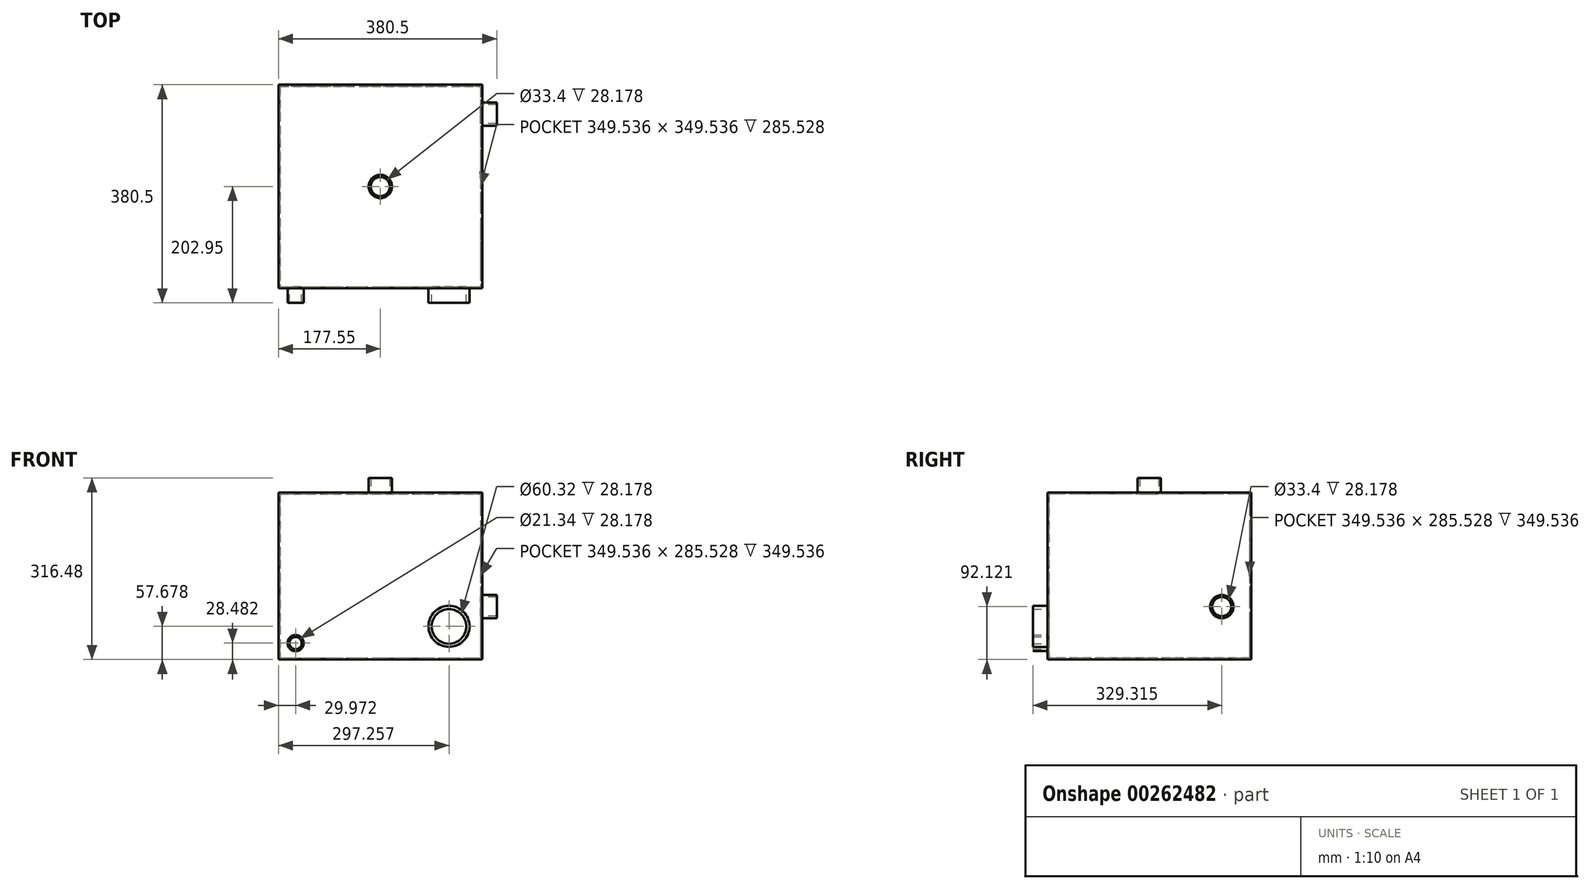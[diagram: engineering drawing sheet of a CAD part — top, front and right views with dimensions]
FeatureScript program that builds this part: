
annotation { "Feature Type Name" : "Feature", "Feature Type Description" : "" }
export const myFeature = defineFeature(function(context is Context, id is Id, definition is map)
    precondition{}
    {
        {
            var Q0;
            Q0=qCreatedBy(makeId("Top.planeOp"),FACE);
            var sketch = newSketch(context, id + "F0", { "sketchPlane" : qUnion([Q0])});
            skLineSegment(sketch, "E0.bottom", {"start": v(-177.55, 177.55) * mm, "end": v(177.55, 177.55) * mm});
            skLineSegment(sketch, "E0.top", {"start": v(-177.55, -177.55) * mm, "end": v(177.55, -177.55) * mm});
            skLineSegment(sketch, "E0.left", {"start": v(-177.55, 177.55) * mm, "end": v(-177.55, -177.55) * mm});
            skLineSegment(sketch, "E0.right", {"start": v(177.55, 177.55) * mm, "end": v(177.55, -177.55) * mm});
            skPoint(sketch, "E0.middle", {"position": v(0, 0) * mm});
            skLineSegment(sketch, "E1.0", {"start": v(174.77, 174.77) * mm, "end": v(174.77, -174.77) * mm});
            skLineSegment(sketch, "E1.1", {"start": v(-174.77, 174.77) * mm, "end": v(174.77, 174.77) * mm});
            skLineSegment(sketch, "E1.2", {"start": v(-174.77, 174.77) * mm, "end": v(-174.77, -174.77) * mm});
            skLineSegment(sketch, "E1.3", {"start": v(-174.77, -174.77) * mm, "end": v(174.77, -174.77) * mm});
            skSolve(sketch);
        }
        {
            var Q0;
            Q0 = qSketchRegion(id + "F0", true);
            extrude(context, id + "F1", {"entities" : qUnion([Q0]), "depth" : 291.08 * mm});
        }
        {
            var Q0;
            Q0=qCreatedBy(makeId("Top.planeOp"),FACE);
            var sketch = newSketch(context, id + "F2", { "sketchPlane" : qUnion([Q0])});
            skLineSegment(sketch, "E2.0", {"start": v(-174.77, 174.77) * mm, "end": v(174.77, 174.77) * mm});
            skLineSegment(sketch, "E2.1", {"start": v(-174.77, 174.77) * mm, "end": v(-174.77, -174.77) * mm});
            skLineSegment(sketch, "E2.2", {"start": v(-174.77, -174.77) * mm, "end": v(174.77, -174.77) * mm});
            skLineSegment(sketch, "E2.3", {"start": v(174.77, 174.77) * mm, "end": v(174.77, -174.77) * mm});
            skSolve(sketch);
        }
        {
            var Q0;
            Q0 = qSketchRegion(id + "F2", true);
            extrude(context, id + "F3", {"entities" : qUnion([Q0]), "operationType" : NewBodyOperationType.ADD, "depth" : 2.78 * mm});
        }
        {
            var Q0;
            Q0=makeQuery(id+"F1.opExtrude","SWEPT_FACE",FACE,{"disambiguationData":[OSD([sQuery(id+"F0.wireOp",EDGE,"E0.top")])]});
            var sketch = newSketch(context, id + "F4", { "sketchPlane" : qUnion([Q0])});
            skCircle(sketch, "E3", {"center": v(119.7, 57.68) * mm, "radius": 30.16 * mm});
            skCircle(sketch, "E4", {"center": v(119.7, 57.68) * mm, "radius": 35.77 * mm});
            skSolve(sketch);
        }
        {
            var Q0;
            Q0 = qSketchRegion(id + "F4", true);
            extrude(context, id + "F5", {"entities" : qUnion([Q0]), "operationType" : NewBodyOperationType.ADD, "depth" : 25.4 * mm});
        }
        {
            var Q0;
            Q0=makeQuery(id+"F5.boolean.opBoolean","SPLIT",FACE,{"disambiguationData":[TD([makeQuery(id+"F5.opExtrude","SWEPT_FACE",FACE,{"disambiguationData":[OSD([sQuery(id+"F4.wireOp",EDGE,"w2y7WUbF-v39G-EkZH-f1oj-RHrdTK3vwLKV")])]})])],"derivedFrom":makeQuery(id+"F1.opExtrude","SWEPT_FACE",FACE,{"disambiguationData":[OSD([sQuery(id+"F0.wireOp",EDGE,"E0.top")])]})});
            var Q1;
            Q1=makeQuery(id+"F5.boolean.opBoolean","SPLIT",FACE,{"disambiguationData":[TD([makeQuery(id+"F5.opExtrude","SWEPT_FACE",FACE,{"disambiguationData":[OSD([sQuery(id+"F4.wireOp",EDGE,"E3")])]})])],"derivedFrom":makeQuery(id+"F1.opExtrude","SWEPT_FACE",FACE,{"disambiguationData":[OSD([sQuery(id+"F0.wireOp",EDGE,"E0.top")])]})});
            extrude(context, id + "F6", {"entities" : qUnion([Q0, Q1]), "operationType" : NewBodyOperationType.REMOVE, "oppositeDirection" : true, "depth" : 25.4 * mm});
        }
        {
            var Q0;
            Q0=makeQuery(id+"F1.opExtrude","SWEPT_FACE",FACE,{"disambiguationData":[OSD([sQuery(id+"F0.wireOp",EDGE,"E0.right")])]});
            var sketch = newSketch(context, id + "F7", { "sketchPlane" : qUnion([Q0])});
            skCircle(sketch, "E5", {"center": v(126.36, 92.12) * mm, "radius": 16.7 * mm});
            skCircle(sketch, "E6", {"center": v(126.36, 92.12) * mm, "radius": 20.3 * mm});
            skSolve(sketch);
        }
        {
            var Q0;
            Q0 = qSketchRegion(id + "F7", true);
            extrude(context, id + "F8", {"entities" : qUnion([Q0]), "operationType" : NewBodyOperationType.ADD, "depth" : 25.4 * mm});
        }
        {
            var Q0;
            Q0=makeQuery(id+"F8.boolean.opBoolean","SPLIT",FACE,{"disambiguationData":[TD([makeQuery(id+"F8.opExtrude","SWEPT_FACE",FACE,{"disambiguationData":[OSD([sQuery(id+"F7.wireOp",EDGE,"E5")])]})])],"derivedFrom":makeQuery(id+"F1.opExtrude","SWEPT_FACE",FACE,{"disambiguationData":[OSD([sQuery(id+"F0.wireOp",EDGE,"E0.right")])]})});
            extrude(context, id + "F9", {"entities" : qUnion([Q0]), "operationType" : NewBodyOperationType.REMOVE, "oppositeDirection" : true, "depth" : 25.4 * mm});
        }
        {
            var Q0;
            {var subQ1=sQuery(id+"F0.wireOp",EDGE,"E0.left");var subQ6=sQuery(id+"F0.wireOp",EDGE,"E0.top");Q0=makeQuery(id+"F5.boolean.opBoolean","SPLIT",FACE,{"disambiguationData":[TD([makeQuery(id+"F1.opExtrude","SWEPT_FACE",FACE,{"disambiguationData":[OSD([subQ1])]})])],"derivedFrom":makeQuery(id+"F1.opExtrude","SWEPT_FACE",FACE,{"disambiguationData":[OSD([subQ6])]})});}
            var sketch = newSketch(context, id + "F10", { "sketchPlane" : qUnion([Q0])});
            skCircle(sketch, "E7", {"center": v(-147.58, 28.48) * mm, "radius": 10.67 * mm});
            skCircle(sketch, "E8", {"center": v(-147.58, 28.48) * mm, "radius": 14.06 * mm});
            skSolve(sketch);
        }
        {
            var Q0;
            Q0 = qSketchRegion(id + "F10", true);
            extrude(context, id + "F11", {"entities" : qUnion([Q0]), "operationType" : NewBodyOperationType.ADD, "depth" : 25.4 * mm});
        }
        {
            var Q0;
            {var subQ1=sQuery(id+"F0.wireOp",EDGE,"E0.left");var subQ6=sQuery(id+"F0.wireOp",EDGE,"E0.top");Q0=makeQuery(id+"F11.boolean.opBoolean","SPLIT",FACE,{"disambiguationData":[TD([makeQuery(id+"F11.opExtrude","SWEPT_FACE",FACE,{"disambiguationData":[OSD([sQuery(id+"F10.wireOp",EDGE,"E7")])]})])],"derivedFrom":makeQuery(id+"F5.boolean.opBoolean","SPLIT",FACE,{"disambiguationData":[TD([makeQuery(id+"F1.opExtrude","SWEPT_FACE",FACE,{"disambiguationData":[OSD([subQ1])]})])],"derivedFrom":makeQuery(id+"F1.opExtrude","SWEPT_FACE",FACE,{"disambiguationData":[OSD([subQ6])]})})});}
            extrude(context, id + "F12", {"entities" : qUnion([Q0]), "operationType" : NewBodyOperationType.REMOVE, "oppositeDirection" : true, "depth" : 25.4 * mm});
        }
        {
            var Q0;
            Q0=makeQuery(id+"F1.opExtrude","CAP_FACE",FACE,{"disambiguationData":[OSD([sQuery(id+"F0.wireOp",EDGE,"E0.bottom"),sQuery(id+"F0.wireOp",EDGE,"E0.top"),sQuery(id+"F0.wireOp",EDGE,"E0.left"),sQuery(id+"F0.wireOp",EDGE,"E0.right"),sQuery(id+"F0.wireOp",EDGE,"E1.0"),sQuery(id+"F0.wireOp",EDGE,"E1.1"),sQuery(id+"F0.wireOp",EDGE,"E1.2"),sQuery(id+"F0.wireOp",EDGE,"E1.3")])],"isStart":false});
            var sketch = newSketch(context, id + "F13", { "sketchPlane" : qUnion([Q0])});
            skLineSegment(sketch, "E9.0", {"start": v(-174.77, 174.77) * mm, "end": v(-174.77, -174.77) * mm});
            skLineSegment(sketch, "E9.1", {"start": v(-174.77, 174.77) * mm, "end": v(174.77, 174.77) * mm});
            skLineSegment(sketch, "E9.2", {"start": v(174.77, 174.77) * mm, "end": v(174.77, -174.77) * mm});
            skLineSegment(sketch, "E9.3", {"start": v(-174.77, -174.77) * mm, "end": v(174.77, -174.77) * mm});
            skSolve(sketch);
        }
        {
            var Q0;
            Q0 = qSketchRegion(id + "F13", true);
            extrude(context, id + "F14", {"entities" : qUnion([Q0]), "operationType" : NewBodyOperationType.ADD, "oppositeDirection" : true, "depth" : 2.78 * mm});
        }
        {
            var Q0;
            Q0=makeQuery(id+"F14.boolean.opBoolean","MERGE",FACE,{"derivedFrom":[makeQuery(id+"F1.opExtrude","CAP_FACE",FACE,{"disambiguationData":[OSD([sQuery(id+"F0.wireOp",EDGE,"E0.bottom"),sQuery(id+"F0.wireOp",EDGE,"E0.top"),sQuery(id+"F0.wireOp",EDGE,"E0.left"),sQuery(id+"F0.wireOp",EDGE,"E0.right"),sQuery(id+"F0.wireOp",EDGE,"E1.0"),sQuery(id+"F0.wireOp",EDGE,"E1.1"),sQuery(id+"F0.wireOp",EDGE,"E1.2"),sQuery(id+"F0.wireOp",EDGE,"E1.3")])],"isStart":false}),makeQuery(id+"F14.opExtrude","CAP_FACE",FACE,{"disambiguationData":[OSD([sQuery(id+"F13.wireOp",EDGE,"E9.0"),sQuery(id+"F13.wireOp",EDGE,"E9.1"),sQuery(id+"F13.wireOp",EDGE,"E9.2"),sQuery(id+"F13.wireOp",EDGE,"E9.3")])],"isStart":true})]});
            var sketch = newSketch(context, id + "F15", { "sketchPlane" : qUnion([Q0])});
            skCircle(sketch, "E10", {"center": v(0, 0) * mm, "radius": 16.7 * mm});
            skCircle(sketch, "E11", {"center": v(0, 0) * mm, "radius": 20.3 * mm});
            skSolve(sketch);
        }
        {
            var Q0;
            Q0 = qSketchRegion(id + "F15", true);
            extrude(context, id + "F16", {"entities" : qUnion([Q0]), "operationType" : NewBodyOperationType.ADD, "depth" : 25.4 * mm});
        }
        {
            var Q0;
            Q0=makeQuery(id+"F16.boolean.opBoolean","SPLIT",FACE,{"disambiguationData":[TD([makeQuery(id+"F16.opExtrude","SWEPT_FACE",FACE,{"disambiguationData":[OSD([sQuery(id+"F15.wireOp",EDGE,"tjWDBAxN-H6gD-sxqh-Nb1s-p2iOPQU3qiK9")])]})])],"derivedFrom":makeQuery(id+"F14.boolean.opBoolean","MERGE",FACE,{"derivedFrom":[makeQuery(id+"F1.opExtrude","CAP_FACE",FACE,{"disambiguationData":[OSD([sQuery(id+"F0.wireOp",EDGE,"E0.bottom"),sQuery(id+"F0.wireOp",EDGE,"E0.top"),sQuery(id+"F0.wireOp",EDGE,"E0.left"),sQuery(id+"F0.wireOp",EDGE,"E0.right"),sQuery(id+"F0.wireOp",EDGE,"E1.0"),sQuery(id+"F0.wireOp",EDGE,"E1.1"),sQuery(id+"F0.wireOp",EDGE,"E1.2"),sQuery(id+"F0.wireOp",EDGE,"E1.3")])],"isStart":false}),makeQuery(id+"F14.opExtrude","CAP_FACE",FACE,{"disambiguationData":[OSD([sQuery(id+"F13.wireOp",EDGE,"E9.0"),sQuery(id+"F13.wireOp",EDGE,"E9.1"),sQuery(id+"F13.wireOp",EDGE,"E9.2"),sQuery(id+"F13.wireOp",EDGE,"E9.3")])],"isStart":true})]})});
            var Q1;
            Q1=makeQuery(id+"F16.boolean.opBoolean","SPLIT",FACE,{"disambiguationData":[TD([makeQuery(id+"F16.opExtrude","SWEPT_FACE",FACE,{"disambiguationData":[OSD([sQuery(id+"F15.wireOp",EDGE,"E10")])]})])],"derivedFrom":makeQuery(id+"F14.boolean.opBoolean","MERGE",FACE,{"derivedFrom":[makeQuery(id+"F1.opExtrude","CAP_FACE",FACE,{"disambiguationData":[OSD([sQuery(id+"F0.wireOp",EDGE,"E0.bottom"),sQuery(id+"F0.wireOp",EDGE,"E0.top"),sQuery(id+"F0.wireOp",EDGE,"E0.left"),sQuery(id+"F0.wireOp",EDGE,"E0.right"),sQuery(id+"F0.wireOp",EDGE,"E1.0"),sQuery(id+"F0.wireOp",EDGE,"E1.1"),sQuery(id+"F0.wireOp",EDGE,"E1.2"),sQuery(id+"F0.wireOp",EDGE,"E1.3")])],"isStart":false}),makeQuery(id+"F14.opExtrude","CAP_FACE",FACE,{"disambiguationData":[OSD([sQuery(id+"F13.wireOp",EDGE,"E9.0"),sQuery(id+"F13.wireOp",EDGE,"E9.1"),sQuery(id+"F13.wireOp",EDGE,"E9.2"),sQuery(id+"F13.wireOp",EDGE,"E9.3")])],"isStart":true})]})});
            extrude(context, id + "F17", {"entities" : qUnion([Q0, Q1]), "operationType" : NewBodyOperationType.REMOVE, "oppositeDirection" : true, "depth" : 25.4 * mm});
        }
    });
